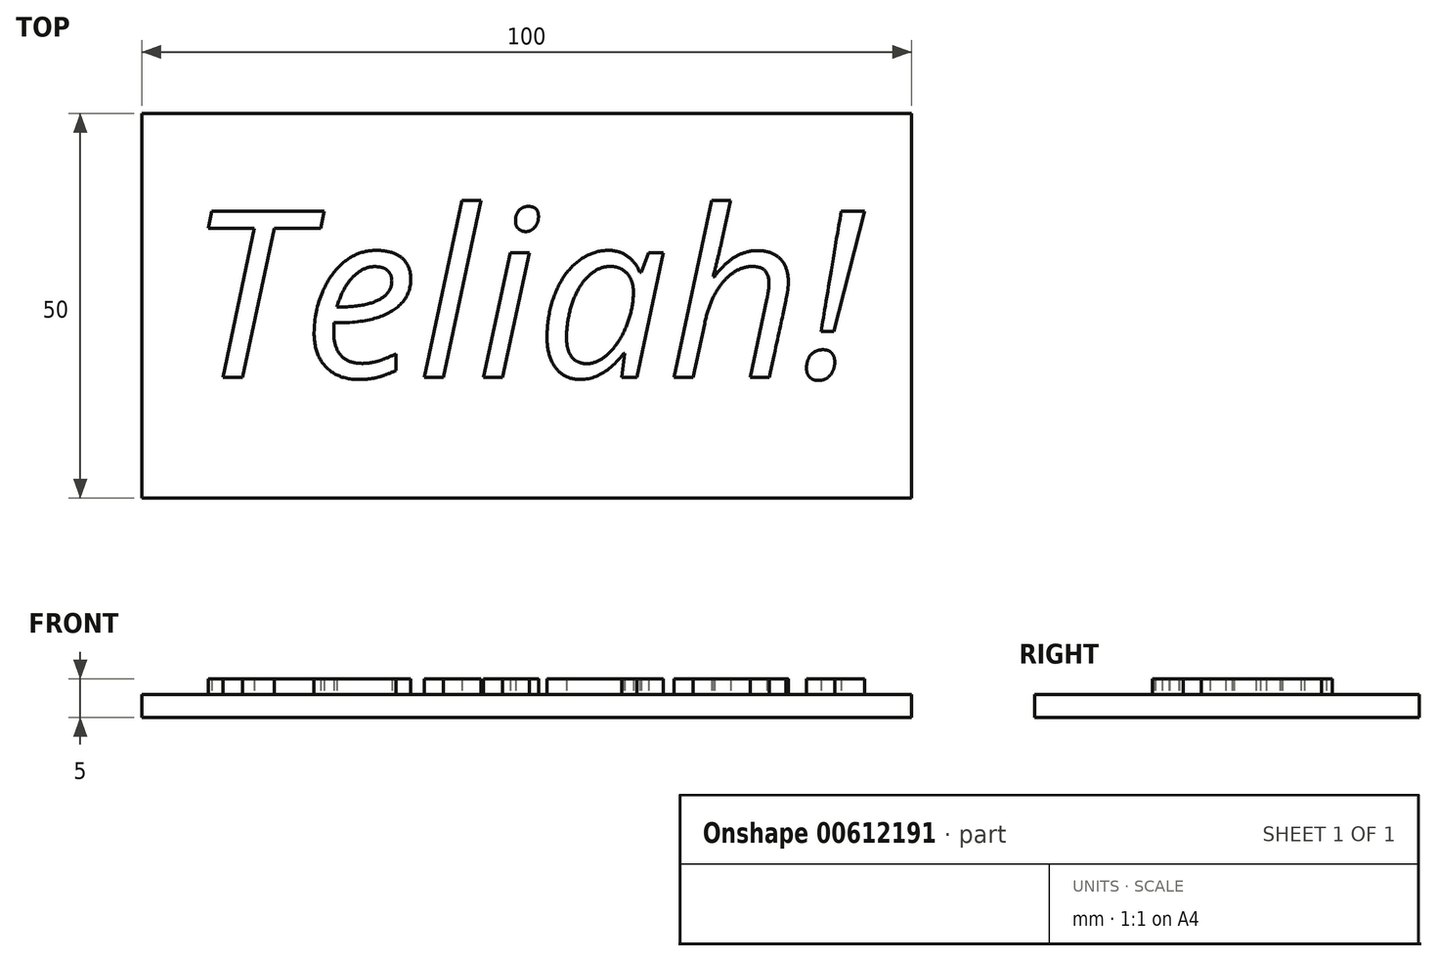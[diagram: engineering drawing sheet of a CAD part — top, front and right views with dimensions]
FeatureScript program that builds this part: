
annotation { "Feature Type Name" : "Feature", "Feature Type Description" : "" }
export const myFeature = defineFeature(function(context is Context, id is Id, definition is map)
    precondition{}
    {
        {
            var Q0;
            Q0=qCreatedBy(makeId("Top.planeOp"),FACE);
            var sketch = newSketch(context, id + "F0", { "sketchPlane" : qUnion([Q0])});
            skLineSegment(sketch, "E0.bottom", {"start": v(0, 0) * mm, "end": v(-100, 0) * mm});
            skLineSegment(sketch, "E0.top", {"start": v(0, 50) * mm, "end": v(-100, 50) * mm});
            skLineSegment(sketch, "E0.left", {"start": v(0, 0) * mm, "end": v(0, 50) * mm});
            skLineSegment(sketch, "E0.right", {"start": v(-100, 0) * mm, "end": v(-100, 50) * mm});
            skSolve(sketch);
        }
        {
            var Q0;
            Q0=makeQuery(id+"F0.imprint","IMPRINT",FACE,{"disambiguationData":[TD([[makeQuery(id+"F0.imprint","IMPRINT",EDGE,{"derivedFrom":sQuery(id+"F0.wireOp",EDGE,"E0.bottom")}),-1.0]])]});
            extrude(context, id + "F1", {"entities" : qUnion([Q0]), "depth" : 3 * mm, "offsetDistance" : 25 * mm});
        }
        {
            var Q0;
            Q0=makeQuery(id+"F1.opExtrude","CAP_FACE",FACE,{"disambiguationData":[OSD([sQuery(id+"F0.wireOp",EDGE,"E0.bottom"),sQuery(id+"F0.wireOp",EDGE,"E0.top"),sQuery(id+"F0.wireOp",EDGE,"E0.left"),sQuery(id+"F0.wireOp",EDGE,"E0.right")])],"isStart":false});
            var sketch = newSketch(context, id + "F2", { "sketchPlane" : qUnion([Q0])});
            skText(sketch, "E1", { "text": "Teliah!", "fontName": "OpenSans-Italic.ttf"});
            const initialGuessF2  = {"E1": [-0.09413, 0.01572, 1, 0, 0.02177]};
            skSetInitialGuess(sketch, initialGuessF2);
            skSolve(sketch);
        }
        {
            var Q0;
            Q0 = qSketchRegion(id + "F2", true);
            extrude(context, id + "F3", {"entities" : qUnion([Q0]), "operationType" : NewBodyOperationType.ADD, "depth" : 2 * mm, "offsetDistance" : 25 * mm});
        }
    });
